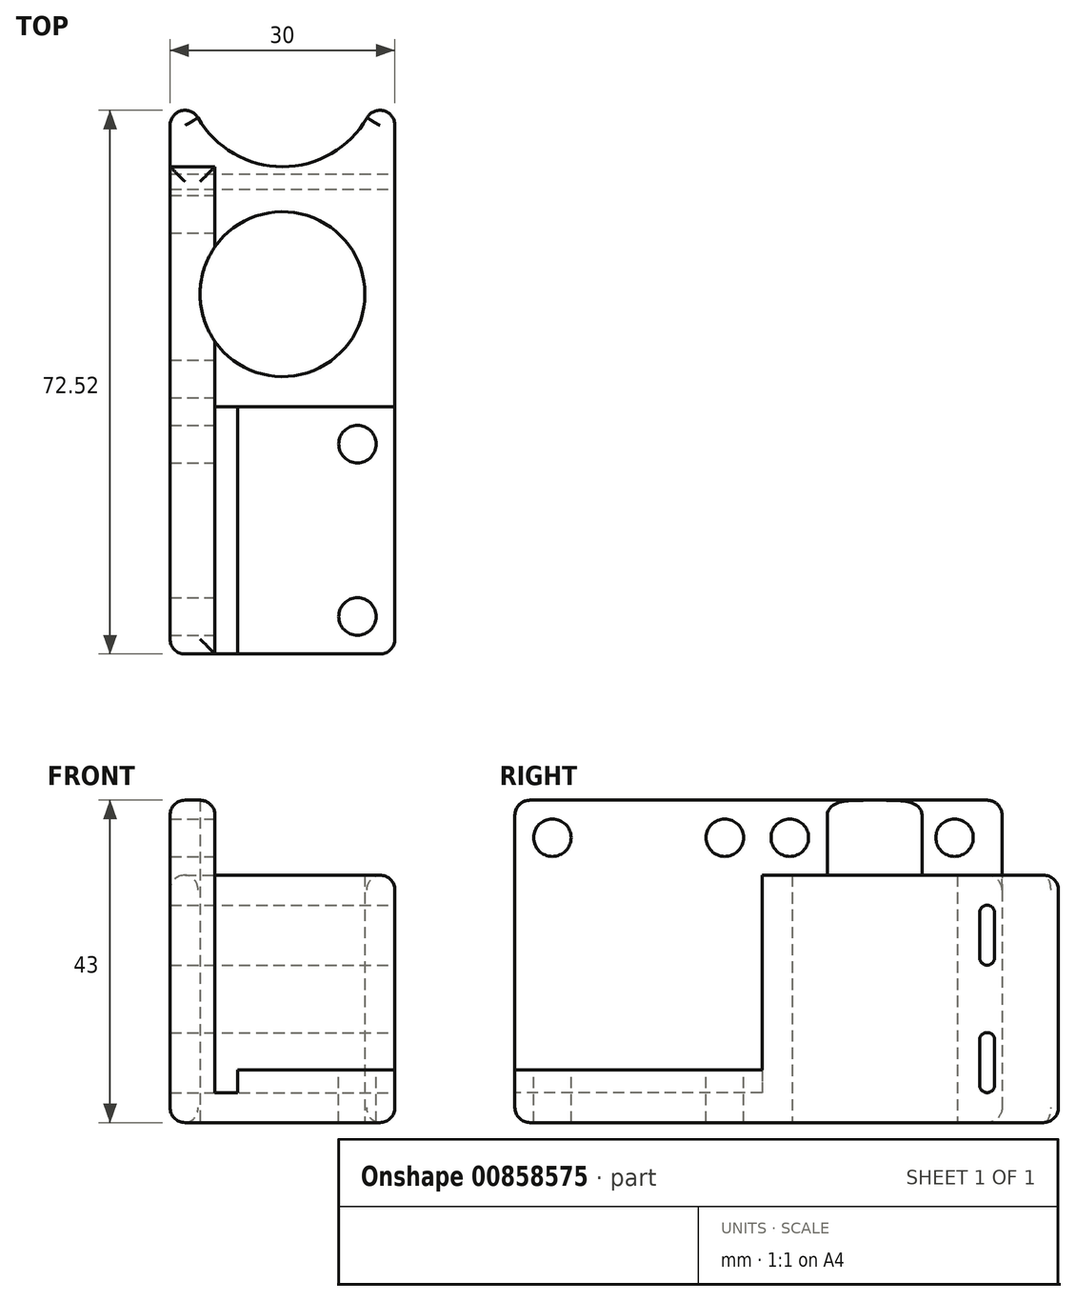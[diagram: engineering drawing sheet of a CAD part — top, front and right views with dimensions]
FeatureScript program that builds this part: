
annotation { "Feature Type Name" : "Feature", "Feature Type Description" : "" }
export const myFeature = defineFeature(function(context is Context, id is Id, definition is map)
    precondition{}
    {
        {
            var Q0;
            Q0=qCreatedBy(makeId("Top.planeOp"),FACE);
            var sketch = newSketch(context, id + "F0", { "sketchPlane" : qUnion([Q0])});
            skCircle(sketch, "E0", {"center": v(0, 0) * mm, "radius": 11 * mm});
            skLineSegment(sketch, "E1.top", {"start": v(-15, 30) * mm, "end": v(-13, 30) * mm});
            skLineSegment(sketch, "E1.left", {"start": v(-15, -48) * mm, "end": v(-15, 30) * mm});
            skLineSegment(sketch, "E1.right", {"start": v(15, -48) * mm, "end": v(15, 30) * mm});
            skLineSegment(sketch, "E2", {"start": v(-15, -48) * mm, "end": v(15, -48) * mm});
            skArc(sketch, "E3", {"start": v(-13, 30) * mm, "mid": v(0, 17) * mm, "end": v(13, 30) * mm});
            skLineSegment(sketch, "E4", {"start": v(13, 30) * mm, "end": v(15, 30) * mm});
            skSolve(sketch);
        }
        {
            var Q0;
            Q0 = qSketchRegion(id + "F0", true);
            extrude(context, id + "F1", {"entities" : qUnion([Q0]), "depth" : 33 * mm, "offsetDistance" : 25 * mm});
        }
        {
            var Q0;
            Q0=makeQuery(id+"F1.opExtrude","SWEPT_FACE",FACE,{"disambiguationData":[OSD([sQuery(id+"F0.wireOp",EDGE,"E2")])]});
            var sketch = newSketch(context, id + "F2", { "sketchPlane" : qUnion([Q0])});
            skSolve(sketch);
        }
        {
            var Q0;
            {var subQ0=sQuery(id+"F0.wireOp",EDGE,"E2");Q0=makeQuery(id+"F2.imprint","IMPRINT",FACE,{"disambiguationData":[TD([[makeQuery(id+"F2.imprint","IMPRINT",EDGE,{"derivedFrom":makeQuery(id+"F1.opExtrude","CAP_EDGE",EDGE,{"disambiguationData":[OSD([subQ0])],"isStart":true})}),1.0]])]});}
            var sketch = newSketch(context, id + "F3", { "sketchPlane" : qUnion([Q0])});
            skLineSegment(sketch, "E5.bottom", {"start": v(-9, 33) * mm, "end": v(15, 33) * mm});
            skLineSegment(sketch, "E5.top", {"start": v(-6, 7) * mm, "end": v(15, 7) * mm});
            skLineSegment(sketch, "E5.left", {"start": v(-9, 33) * mm, "end": v(-9, 7) * mm});
            skLineSegment(sketch, "E5.right", {"start": v(15, 33) * mm, "end": v(15, 7) * mm});
            skLineSegment(sketch, "E6.bottom", {"start": v(-9, 7) * mm, "end": v(-6, 7) * mm});
            skLineSegment(sketch, "E6.top", {"start": v(-9, 4) * mm, "end": v(-6, 4) * mm});
            skLineSegment(sketch, "E6.left", {"start": v(-9, 7) * mm, "end": v(-9, 4) * mm});
            skLineSegment(sketch, "E6.right", {"start": v(-6, 7) * mm, "end": v(-6, 4) * mm});
            skSolve(sketch);
        }
        {
            var Q0;
            Q0 = qSketchRegion(id + "F3", true);
            extrude(context, id + "F4", {"entities" : qUnion([Q0]), "operationType" : NewBodyOperationType.REMOVE, "oppositeDirection" : true, "depth" : 33 * mm, "offsetDistance" : 25 * mm});
        }
        {
            var Q0;
            Q0=makeQuery(id+"F4.boolean.opBoolean","COPY",FACE,{"derivedFrom":makeQuery(id+"F4.opExtrude","SWEPT_FACE",FACE,{"disambiguationData":[OSD([sQuery(id+"F3.wireOp",EDGE,"E5.top")])]})});
            var sketch = newSketch(context, id + "F5", { "sketchPlane" : qUnion([Q0])});
            skPoint(sketch, "E7", {"position": v(10, -20) * mm});
            skPoint(sketch, "E8", {"position": v(10, -43) * mm});
            skSolve(sketch);
        }
        {
            var Q0;
            Q0=sQuery(id+"F5.wireOp",VERTEX,"E7");
            var Q1;
            Q1=sQuery(id+"F5.wireOp",VERTEX,"E8");
            var Q2;
            Q2=makeQuery(id+"F1.opExtrude","SWEPT_BODY",BODY,{"disambiguationData":[OSD([sQuery(id+"F0.wireOp",EDGE,"E0"),sQuery(id+"F0.wireOp",EDGE,"E1.top"),sQuery(id+"F0.wireOp",EDGE,"E1.left"),sQuery(id+"F0.wireOp",EDGE,"E1.right"),sQuery(id+"F0.wireOp",EDGE,"E2"),sQuery(id+"F0.wireOp",EDGE,"E3"),sQuery(id+"F0.wireOp",EDGE,"E4")])]});
            hole(context, id + "F6", {"style" : HoleStyle.SIMPLE, "endStyle" : HoleEndStyle.BLIND, "holeDiameter" : 5 * mm, "majorDiameter" : 5 * mm, "holeDepth" : 10 * mm, "isTappedThrough" : true, "tappedDepth" : 12 * mm, "tapClearance" : 3, "startFromSketch" : true, "locations" : qUnion([Q0, Q1]), "scope" : qUnion([Q2])});
        }
        {
            var Q0;
            Q0=makeQuery(id+"F1.opExtrude","CAP_FACE",FACE,{"disambiguationData":[OSD([sQuery(id+"F0.wireOp",EDGE,"E0"),sQuery(id+"F0.wireOp",EDGE,"E1.top"),sQuery(id+"F0.wireOp",EDGE,"E1.left"),sQuery(id+"F0.wireOp",EDGE,"E1.right"),sQuery(id+"F0.wireOp",EDGE,"E2"),sQuery(id+"F0.wireOp",EDGE,"E3"),sQuery(id+"F0.wireOp",EDGE,"E4")])],"isStart":false});
            var sketch = newSketch(context, id + "F7", { "sketchPlane" : qUnion([Q0])});
            skPoint(sketch, "E9.oppositeSnap0", {"position": v(0, 17) * mm});
            skLineSegment(sketch, "E9.bottom", {"start": v(-15, -48) * mm, "end": v(-9, -48) * mm});
            skLineSegment(sketch, "E9.top", {"start": v(-15, 17) * mm, "end": v(-9, 17) * mm});
            skLineSegment(sketch, "E9.left", {"start": v(-15, -48) * mm, "end": v(-15, 17) * mm});
            skLineSegment(sketch, "E9.right", {"start": v(-9, -48) * mm, "end": v(-9, -6.32) * mm});
            skArc(sketch, "E10", {"start": v(-9, 6.32) * mm, "mid": v(-11, 0) * mm, "end": v(-9, -6.32) * mm});
            skLineSegment(sketch, "E11", {"start": v(-9, 6.32) * mm, "end": v(-9, 17) * mm});
            skSolve(sketch);
        }
        {
            var Q0;
            Q0 = qSketchRegion(id + "F7", true);
            extrude(context, id + "F8", {"entities" : qUnion([Q0]), "operationType" : NewBodyOperationType.ADD, "depth" : 10 * mm, "offsetDistance" : 25 * mm});
        }
        {
            var Q0;
            Q0=makeQuery(id+"F8.boolean.opBoolean","MERGE",FACE,{"derivedFrom":[makeQuery(id+"F4.boolean.opBoolean","COPY",FACE,{"derivedFrom":makeQuery(id+"F4.opExtrude","SWEPT_FACE",FACE,{"disambiguationData":[OSD([sQuery(id+"F3.wireOp",EDGE,"E5.left"),sQuery(id+"F3.wireOp",EDGE,"E6.left")])]})}),makeQuery(id+"F8.opExtrude","SWEPT_FACE",FACE,{"disambiguationData":[OSD([sQuery(id+"F7.wireOp",EDGE,"E9.right")])]})]});
            var sketch = newSketch(context, id + "F9", { "sketchPlane" : qUnion([Q0])});
            skPoint(sketch, "E12", {"position": v(-43, 38) * mm});
            skPoint(sketch, "E13", {"position": v(-20, 38) * mm});
            skPoint(sketch, "E14", {"position": v(-11.32, 38) * mm});
            skSolve(sketch);
        }
        {
            var Q0;
            Q0=makeQuery(id+"F8.opExtrude","SWEPT_FACE",FACE,{"disambiguationData":[OSD([sQuery(id+"F7.wireOp",EDGE,"E11")])]});
            var sketch = newSketch(context, id + "F10", { "sketchPlane" : qUnion([Q0])});
            skPoint(sketch, "E15", {"position": v(10.65, 38) * mm});
            skSolve(sketch);
        }
        {
            var Q0;
            Q0=sQuery(id+"F10.wireOp",VERTEX,"E15");
            var Q1;
            Q1=sQuery(id+"F9.wireOp",VERTEX,"E14");
            var Q2;
            Q2=sQuery(id+"F9.wireOp",VERTEX,"E13");
            var Q3;
            Q3=sQuery(id+"F9.wireOp",VERTEX,"E12");
            var Q4;
            Q4=makeQuery(id+"F1.opExtrude","SWEPT_BODY",BODY,{"disambiguationData":[OSD([sQuery(id+"F0.wireOp",EDGE,"E0"),sQuery(id+"F0.wireOp",EDGE,"E1.top"),sQuery(id+"F0.wireOp",EDGE,"E1.left"),sQuery(id+"F0.wireOp",EDGE,"E1.right"),sQuery(id+"F0.wireOp",EDGE,"E2"),sQuery(id+"F0.wireOp",EDGE,"E3"),sQuery(id+"F0.wireOp",EDGE,"E4")])]});
            hole(context, id + "F11", {"style" : HoleStyle.SIMPLE, "endStyle" : HoleEndStyle.BLIND, "holeDiameter" : 5 * mm, "majorDiameter" : 5 * mm, "holeDepth" : 10 * mm, "isTappedThrough" : true, "tappedDepth" : 12 * mm, "tapClearance" : 3, "startFromSketch" : true, "locations" : qUnion([Q0, Q1, Q2, Q3]), "scope" : qUnion([Q4])});
        }
        {
            var Q0;
            Q0=makeQuery(id+"F1.opExtrude","SWEPT_FACE",FACE,{"disambiguationData":[OSD([sQuery(id+"F0.wireOp",EDGE,"E1.right")])]});
            var sketch = newSketch(context, id + "F12", { "sketchPlane" : qUnion([Q0])});
            skLineSegment(sketch, "E16.left", {"start": v(14, 28) * mm, "end": v(14, 22) * mm});
            skLineSegment(sketch, "E16.right", {"start": v(16, 28) * mm, "end": v(16, 22) * mm});
            skLineSegment(sketch, "E17.left", {"start": v(14, 11) * mm, "end": v(14, 5) * mm});
            skLineSegment(sketch, "E17.right", {"start": v(16, 11) * mm, "end": v(16, 5) * mm});
            skArc(sketch, "E18", {"start": v(16, 28) * mm, "mid": v(15, 29) * mm, "end": v(14, 28) * mm});
            skArc(sketch, "E19", {"start": v(14, 22) * mm, "mid": v(15, 21) * mm, "end": v(16, 22) * mm});
            skArc(sketch, "E20", {"start": v(16, 11) * mm, "mid": v(15, 12) * mm, "end": v(14, 11) * mm});
            skArc(sketch, "E21", {"start": v(14, 5) * mm, "mid": v(15, 4) * mm, "end": v(16, 5) * mm});
            skSolve(sketch);
        }
        {
            var Q0;
            Q0 = qSketchRegion(id + "F12", true);
            extrude(context, id + "F13", {"entities" : qUnion([Q0]), "operationType" : NewBodyOperationType.REMOVE, "oppositeDirection" : true, "depth" : 30 * mm, "offsetDistance" : 25 * mm});
        }
        {
            var Q0;
            Q0=makeQuery(id+"F1.opExtrude","CAP_EDGE",EDGE,{"disambiguationData":[OSD([sQuery(id+"F0.wireOp",EDGE,"E3")])],"isStart":true});
            var Q1;
            Q1=makeQuery(id+"F1.opExtrude","CAP_EDGE",EDGE,{"disambiguationData":[OSD([sQuery(id+"F0.wireOp",EDGE,"E3")])],"isStart":false});
            fillet(context, id + "F14", {"entities" : qUnion([Q0, Q1]), "radius" : 2 * mm, "tangentPropagation" : true, "allowEdgeOverflow" : false});
        }
        {
            var Q0;
            Q0=makeQuery(id+"F1.opExtrude","SWEPT_EDGE",EDGE,{"disambiguationData":[OSD([sQuery(id+"F0.wireOp",EDGE,"E1.top"),sQuery(id+"F0.wireOp",EDGE,"E3")])]});
            var Q1;
            Q1=makeQuery(id+"F1.opExtrude","SWEPT_EDGE",EDGE,{"disambiguationData":[OSD([sQuery(id+"F0.wireOp",EDGE,"E3"),sQuery(id+"F0.wireOp",EDGE,"E4")])]});
            fillet(context, id + "F15", {"entities" : qUnion([Q0, Q1]), "radius" : 1 * mm, "tangentPropagation" : true, "allowEdgeOverflow" : false});
        }
        {
            var Q0;
            Q0=makeQuery(id+"F1.opExtrude","CAP_EDGE",EDGE,{"disambiguationData":[OSD([sQuery(id+"F0.wireOp",EDGE,"E1.left")])],"isStart":true});
            var Q1;
            Q1=makeQuery(id+"F1.opExtrude","CAP_EDGE",EDGE,{"disambiguationData":[OSD([sQuery(id+"F0.wireOp",EDGE,"E1.right")])],"isStart":true});
            var Q2;
            Q2=makeQuery(id+"F1.opExtrude","CAP_EDGE",EDGE,{"disambiguationData":[OSD([sQuery(id+"F0.wireOp",EDGE,"E2")])],"isStart":true});
            var Q3;
            Q3=makeQuery(id+"F8.boolean.opBoolean","MERGE",EDGE,{"derivedFrom":[makeQuery(id+"F1.opExtrude","SWEPT_EDGE",EDGE,{"disambiguationData":[OSD([sQuery(id+"F0.wireOp",EDGE,"E1.left"),sQuery(id+"F0.wireOp",EDGE,"E2")])]}),makeQuery(id+"F8.opExtrude","SWEPT_EDGE",EDGE,{"disambiguationData":[OSD([sQuery(id+"F7.wireOp",EDGE,"E9.bottom"),sQuery(id+"F7.wireOp",EDGE,"E9.left")])]})]});
            var Q4;
            Q4=makeQuery(id+"F1.opExtrude","SWEPT_EDGE",EDGE,{"disambiguationData":[OSD([sQuery(id+"F0.wireOp",EDGE,"E1.right"),sQuery(id+"F0.wireOp",EDGE,"E2")])]});
            var Q5;
            Q5=makeQuery(id+"F4.boolean.opBoolean","COPY",EDGE,{"derivedFrom":makeQuery(id+"F4.opExtrude","SWEPT_EDGE",EDGE,{"disambiguationData":[OSD([sQuery(id+"F0.wireOp",EDGE,"E1.right"),sQuery(id+"F0.wireOp",EDGE,"E2"),sQuery(id+"F3.wireOp",EDGE,"E5.top"),sQuery(id+"F3.wireOp",EDGE,"E5.right")])]})});
            var Q6;
            Q6=makeQuery(id+"F4.boolean.opBoolean","COPY",EDGE,{"derivedFrom":makeQuery(id+"F4.opExtrude","CAP_EDGE",EDGE,{"disambiguationData":[OSD([sQuery(id+"F3.wireOp",EDGE,"E5.right")])],"isStart":false})});
            var Q7;
            Q7=makeQuery(id+"F4.boolean.opBoolean","COPY",EDGE,{"derivedFrom":makeQuery(id+"F4.opExtrude","CAP_EDGE",EDGE,{"disambiguationData":[OSD([sQuery(id+"F3.wireOp",EDGE,"E5.bottom")])],"isStart":false})});
            var Q8;
            Q8=makeQuery(id+"F4.boolean.opBoolean","COPY",EDGE,{"derivedFrom":makeQuery(id+"F4.opExtrude","CAP_EDGE",EDGE,{"disambiguationData":[OSD([sQuery(id+"F3.wireOp",EDGE,"E5.top")])],"isStart":true})});
            var Q9;
            Q9=makeQuery(id+"F8.opExtrude","CAP_EDGE",EDGE,{"disambiguationData":[OSD([sQuery(id+"F7.wireOp",EDGE,"E9.bottom")])],"isStart":false});
            var Q10;
            Q10=makeQuery(id+"F8.opExtrude","CAP_EDGE",EDGE,{"disambiguationData":[OSD([sQuery(id+"F7.wireOp",EDGE,"E9.right")])],"isStart":false});
            var Q11;
            Q11=makeQuery(id+"F8.opExtrude","CAP_EDGE",EDGE,{"disambiguationData":[OSD([sQuery(id+"F7.wireOp",EDGE,"E11")])],"isStart":false});
            var Q12;
            Q12=makeQuery(id+"F8.opExtrude","CAP_EDGE",EDGE,{"disambiguationData":[OSD([sQuery(id+"F7.wireOp",EDGE,"E9.top")])],"isStart":false});
            var Q13;
            Q13=makeQuery(id+"F8.opExtrude","CAP_EDGE",EDGE,{"disambiguationData":[OSD([sQuery(id+"F7.wireOp",EDGE,"E9.left")])],"isStart":false});
            fillet(context, id + "F16", {"entities" : qUnion([Q0, Q1, Q2, Q3, Q4, Q5, Q6, Q7, Q8, Q9, Q10, Q11, Q12, Q13]), "radius" : 2 * mm, "tangentPropagation" : true, "allowEdgeOverflow" : false});
        }
    });
